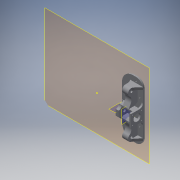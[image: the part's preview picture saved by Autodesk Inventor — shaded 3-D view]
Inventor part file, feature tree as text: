
AUTODESK INVENTOR PART (.ipt)
format: ipt  version: 2016 (Build 200138000, 138)  size: 474,624 bytes
history: native  units: in
note: dims shown in document units (in); Inventor stores cm internally (conversion verified against a paired STEP export)
features: sketch x14, extrude x12, projected_geometry x8, fillet x6, plane x3, chamfer x2, reference x1
ambient origin geometry x8: Origin, YZ Plane, XZ Plane, XY Plane, X Axis, Y Axis, Z Axis, Center Point
bodies: Solid1 (feature_tree)
feature tree (46):
  plane  "Work Plane1"
  extrude  "Extrusion1"  Depth=0.2in TaperAngle=0.0deg
  extrude  "Extrusion2"  TaperAngle=90.0deg  [1 undecoded]
  extrude  "Extrusion3"  Depth=1.7in
  extrude  "Extrusion4"  Depth=0.6102in
  extrude  "Extrusion5"  Depth=0.1181in
  extrude  "Extrusion6"  Depth=0.2362in TaperAngle=0.0deg
  extrude  "Extrusion7"  Depth=0.8in
  plane  "Work Plane2"
  extrude  "Extrusion8"  Depth=1.4961in TaperAngle=0.0deg
  extrude  "Extrusion9"  Depth=0.3937in TaperAngle=0.0deg
  fillet  "Fillet1"  Radius=0.45in
  fillet  "Fillet2"  Radius=0.45in
  fillet  "Fillet3"  Radius=0.45in
  sketch  "Sketch10"  dims[d33=0.45in d34=0.8312in d35=0.0in]
  sketch  "Sketch11"  dims[d36=0.3937in d37=0.0787in d38=0.0in]
  chamfer  "Chamfer1"  Distance=0.8312in
  chamfer  "Chamfer2"  Distance=0.0787in
  extrude  "Extrusion10"  Depth=0.9375in
  extrude  "Extrusion11"  Depth=2.7559in
  plane  "Work Plane3"
  extrude  "Extrusion12"  Depth=0.5in
  fillet  "Fillet4"  Radius=0.315in
  fillet  "Fillet5"  Radius=1.0in
  fillet  "Fillet6"  Radius=1.0in
  sketch  "Sketch1"  dims[d0=8.0in d1=0.2in d2=0.0in]
  reference  "Reference1"
  sketch  "Sketch2"  dims[d3=0.85in d4=90.0deg]
  projected_geometry  "Projected Loop1"
  sketch  "Sketch3"  dims[d5=1.7in d6=1.7in]
  projected_geometry  "Projected Loop2"
  sketch  "Sketch4"  dims[d7=0.9843in d8=0.6102in]
  projected_geometry  "Projected Loop3"
  sketch  "Sketch5"  dims[d9=0.6102in d10=0.1181in]
  projected_geometry  "Projected Loop4"
  sketch  "Sketch6"  dims[d11=0.7874in d13=1.2205in d14=0.7874in d16=1.2205in d19=0.2362in d20=0.0in]
  projected_geometry  "Projected Loop5"
  sketch  "Sketch7"  dims[d21=0.8in d22=0.8in]
  projected_geometry  "Projected Loop6"
  sketch  "Sketch8"  dims[d23=0.8in d24=1.4961in d25=0.0in]
  sketch  "Sketch9"  dims[d26=0.8661in d27=0.3937in d28=0.0in d30=0.45in d31=0.45in d32=0.45in]
  sketch  "Sketch12"  dims[d39=0.4537in d40=0.0in d41=0.9375in]
  projected_geometry  "Projected Loop7"
  sketch  "Sketch13"  dims[d42=0.8287in d43=0.0in d45=2.7559in]
  projected_geometry  "Projected Loop8"
  sketch  "Sketch14"  dims[d46=0.315in d47=2.7559in d48=0.315in d49=1.0in d50=1.0in d51=0.8287in d52=0.0in d53=1.5625in d54=1.0in d55=0.8125in d56=0.1875in d57=0.125in d58=45.0deg d59=0.25in d60=0.125in d61=45.0deg d62=0.3287in d63=0.0in d64=0.3287in d65=0.0in d66=0.6412in d67=0.0in d68=0.8125in d69=0.8125in d70=0.5in]
note: 1 required parameter value undecoded (feature->parameter linkage not recoverable at this tier; creation-order binding heuristic only, values carry confidence <= 0.55)
